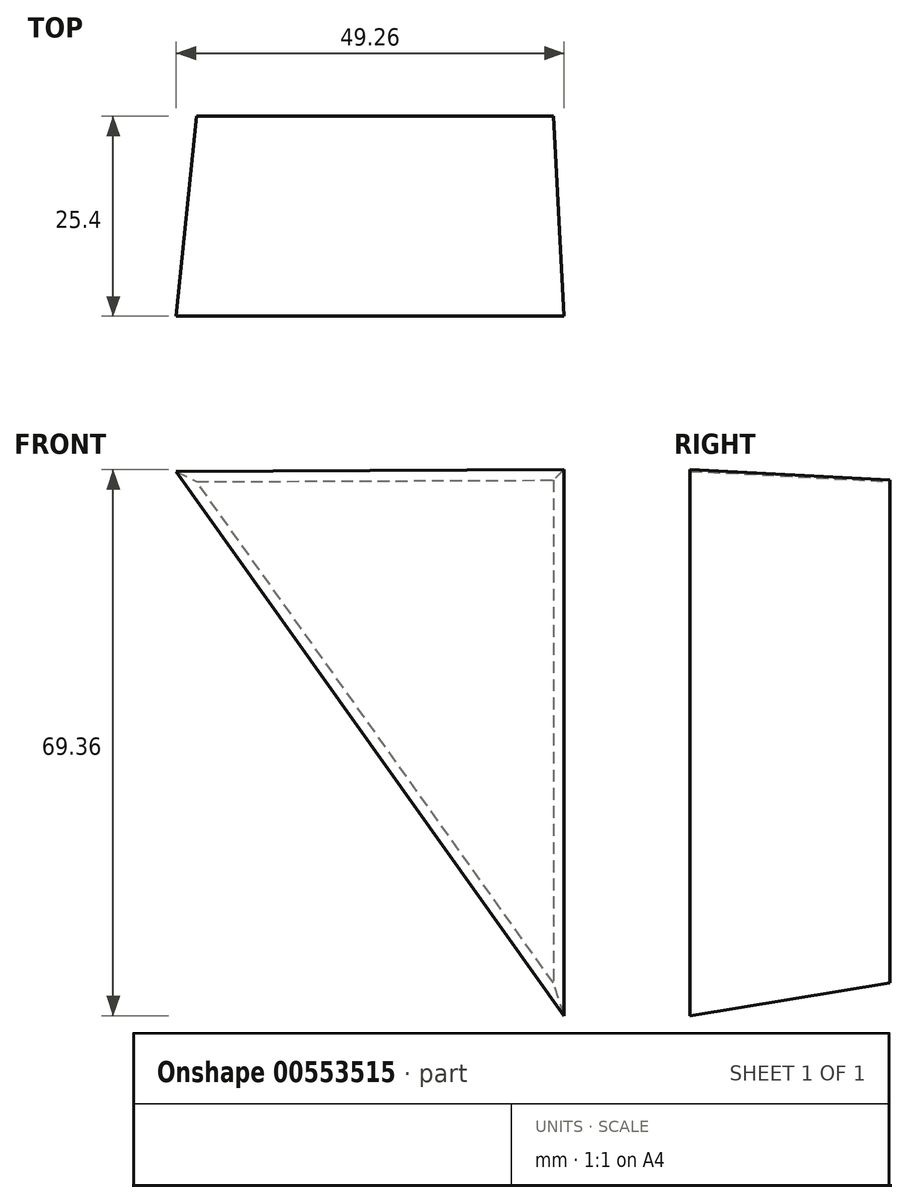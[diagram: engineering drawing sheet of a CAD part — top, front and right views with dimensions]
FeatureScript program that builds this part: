
annotation { "Feature Type Name" : "Feature", "Feature Type Description" : "" }
export const myFeature = defineFeature(function(context is Context, id is Id, definition is map)
    precondition{}
    {
        {
            var Q0;
            Q0=qCreatedBy(makeId("Front.planeOp"),FACE);
            var sketch = newSketch(context, id + "F0", { "sketchPlane" : qUnion([Q0])});
            skLineSegment(sketch, "E0", {"start": v(0, 63.87) * mm, "end": v(0, 0) * mm});
            skLineSegment(sketch, "E1", {"start": v(0, 0) * mm, "end": v(-45.35, 63.68) * mm});
            skLineSegment(sketch, "E2", {"start": v(-45.35, 63.68) * mm, "end": v(0, 63.87) * mm});
            skLineSegment(sketch, "E3", {"start": v(-22.68, 31.84) * mm, "end": v(-95.08, -54.52) * mm, "construction": true});
            skSolve(sketch);
        }
        {
            var Q0;
            Q0 = qSketchRegion(id + "F0", true);
            extrude(context, id + "F1", {"entities" : qUnion([Q0]), "depth" : 25.4 * mm, "offsetDistance" : 25.4 * mm, "hasDraft" : true, "draftAngle" : 3 * degree});
        }
    });
